# Revit family: AM0066621AlacenaPraga
name_source: partatom
category: Specialty Equipment
units: mm (PartAtom-declared; Revit-internal decimal feet)

## family parameters
Always vertical = Yes
Cut with Voids When Loaded = No
OmniClass Number = 23.21.23.00
OmniClass Title = Residential Furniture and Equipment
Part Type = Normal
Room Calculation Point = No
Round Connector Dimension = Use Diameter
Shared = No
Work Plane-Based = No

## types (1)
- AM0066621AlacenaPraga
    Carga máxima = 40 kg.
    Creado por = IDD
    Densidad = 15 mms 670 kg./m^3.   6 mms 742 kg./m^3.
    Fecha de creación = 09/10/2020
    Manufacturer = Corona
    Material Aglomerado = Corona_Madera_Aglomerada_Habano
    Material Interior = Corona_Madera_Aglomerada_Plomo
    Material Patas = Corona_Acabado_Satinado
    Peso Neto aproximado = 47,7 kg.
    Referencia = AM0066621
    Resistencia a la humedad = Hinchamiento < o =8%.
    URL = https://corona.co

## geometry (parser evidence)
native form markers: Sweep x9
no freeform markers — native parametric forms only
